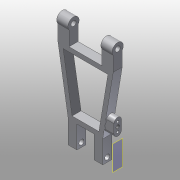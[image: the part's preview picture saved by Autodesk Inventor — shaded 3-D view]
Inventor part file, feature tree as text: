
AUTODESK INVENTOR PART (.ipt)
format: ipt  version: 2016 (Build 200138000, 138)  size: 201,728 bytes
history: native  units: mm
features: sketch x9, extrude x7, hole x3, plane x1
ambient origin geometry x8: Origin, YZ Plane, XZ Plane, XY Plane, X Axis, Y Axis, Z Axis, Center Point
bodies: Solid1 (feature_tree)
feature tree (20):
  extrude  "Extrusion1"  Depth=7.5mm
  extrude  "Extrusion2"  Depth=5.8mm
  extrude  "Extrusion3"  Depth=23.0mm
  extrude  "Extrusion4"  Depth=15.0mm
  extrude  "Extrusion5"  Depth=6.0mm TaperAngle=0.0deg
  extrude  "Extrusion6"  Depth=3.0mm
  hole  "Hole1"  [1 undecoded]
  plane  "Work Plane1"
  extrude  "Extrusion7"  Depth=6.0mm
  hole  "Hole2"  [1 undecoded]
  hole  "Hole3"  [1 undecoded]
  sketch  "Sketch1"  dims[d0=37.0mm d1=7.5mm]
  sketch  "Sketch2"  dims[d2=15.0mm d3=5.8mm]
  sketch  "Sketch3"  dims[d4=23.0mm d5=72.0mm]
  sketch  "Sketch4"  dims[d6=15.0mm d7=15.0mm]
  sketch  "Sketch5"  dims[d8=15.0mm d9=6.0mm d10=0.0mm]
  sketch  "Sketch6"  dims[d11=3.0mm d12=3.0mm]
  sketch  "Sketch7"  dims[d13=3.0mm d14=3.0mm]
  sketch  "Sketch8"  dims[d15=6.0mm d16=0.0mm d17=3.4mm]
  sketch  "Sketch9"  dims[d18=3.0mm d19=6.0mm d20=0.0mm d21=7.5mm d22=3.0mm d23=6.0mm d24=0.0mm d25=6.0mm d26=0.0mm d27=7.5mm d28=6.0mm d29=0.0mm d30=10.0mm d31=10.0mm d32=3.4mm d33=6.0mm d34=4.0mm d35=2.0mm d36=90.0deg d37=46.75mm d38=20.594885mm d39=-30.0mm d40=21.0mm d41=5.0mm d42=6.0mm d43=7.25mm d44=0.0mm d45=1.5mm d46=6.0mm d47=4.0mm d48=2.0mm d49=90.0deg d50=3.0mm d51=20.594885mm d52=2.459mm d53=6.0mm d54=4.0mm d55=2.0mm d56=90.0deg d57=10.8mm d58=20.594885mm]
note: 3 required parameter values undecoded (feature->parameter linkage not recoverable at this tier; creation-order binding heuristic only, values carry confidence <= 0.55)
